# Revit family: PRD_FrankeWS_WstBns_EXOSWasteBin_EXOS605EX_605EB_605EW
name_source: partatom
category: Specialty Equipment
revit_build: Autodesk Revit 2018 (Build: 20190510_1515(x64)
units: mm (PartAtom-declared; Revit-internal decimal feet)

## family parameters
Cut with Voids When Loaded = No
Host = Face
OmniClass Number = 23.40.20.31.11
OmniClass Title = Bins
Part Type = Normal
Room Calculation Point = No
Round Connector Dimension = Use Diameter
Shared = No

## types (3) — shared parameters
AssetType = Fixed
BagHolder = Integrated
Category = Pr_40_50_07_96, Waste bins
Default Elevation = 800 mm  [stored 2.62467 ft]
DispenserMaterial = PRD_AR_StainlessSteel_SatinFinished
DurationUnit = year
Features = stainless steel, surface satin finished
FillingVolume = 30.00 liter
Finish = satin finished
IfcExportAs = IfcFurnitureType
IfcExportType = USERDEFINED
IntegralAccessories = incl. mounting materials
IsBuiltIn = TRUE
Lid = No
Lock = Key-lock
MainColor = stainless steel
Manufacturer = KWC Group AG
ManufacturerName = KWC Group AG
ManufacturerURL = www.kwc.com
Material = stainless steel
MaterialCode = 1.4301
MaterialThickness = 1.20 mm
NBSDescription = Waste bins
NBSReference = 45-35-72/380
NominalDepth = 251 mm  [stored 0.823491 ft]
NominalHeight = 790 mm  [stored 2.59186 ft]
NominalWidth = 304 mm  [stored 0.997375 ft]
ProductInformation = https://pim.kwc.com
Size = 304 x 790 x 251 mm
Style = Waste bin
SurfaceTreatment = InoxPlus (anti fingerprint)
TypeOfFixing = Screw
TypeOfMounting = Recessed mounting
URL = www.kwc.com
Uniclass2015Code = Pr_40_50_07_96
Uniclass2015Title = Waste bins
Uniclass2015Version = Products v1.17
Version = 1
WarrantyDurationUnit = year

## per-type parameters (varying)
| type | BIMObjectName | Description | GrossWeight | ModelNumber | Name | NetWeight | PanelMaterial |
| EXOS605EX | PRD_AR_WasteBins_EXOSWasteBin_EXOS605EX | Waste bin for recessed mounting, stainless steel with satin finish, front and casing with InoxPlus surface refinement for the reduction of finger marks and better cleaning characteristics (easy to clean), material thickness 1.2 mm, capacity approximate 30 litres, integrated bag holder, includes mounting materials. | 12.98 kg | 2030034628 | Waste Bin EXOS605EX | 11.98 kg | PRD_AR_StainlessSteel_SatinFinished |
| EXOS605EB | PRD_AR_WasteBins_EXOSWasteBin_EXOS605EB | Waste bin for recessed mounting, stainless steel with satin finish, black safety glass front panel, casing with InoxPlus surface refinement for the reduction of finger marks and better cleaning characteristics (easy to clean), material thickness 1.2 mm, capacity approximate 30 litres, integrated bag holder, includes mounting materials. | 14.17 kg | 2030034629 | Waste Bin EXOS605EB | 13.17 kg | PRD_AR_Glass_Black |
| EXOS605EW | PRD_AR_WasteBins_EXOSWasteBin_EXOS605EW | Waste bin for recessed mounting, stainless steel with satin finish, white safety glass front panel, casing with InoxPlus surface refinement for the reduction of finger marks and better cleaning characteristics (easy to clean), material thickness 1.2 mm, capacity approximate 30 litres, integrated bag holder, includes mounting materials. | 14.17 kg | 2030034664 | Waste Bin EXOS605EW | 13.17 kg | PRD_AR_Glass_White |

note: column(s) folded — value = type name in every type: Model, ModelReference

note: [stored X ft] marks values corroborated as IEEE doubles in the binary element streams (Revit-internal decimal feet)

## geometry (parser evidence)
native form markers: Sweep x5
no freeform markers — native parametric forms only
